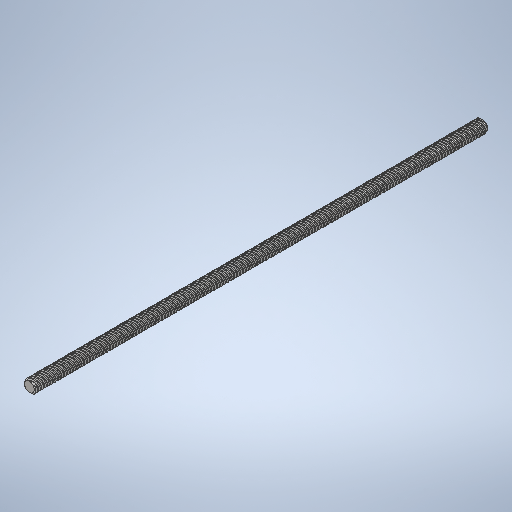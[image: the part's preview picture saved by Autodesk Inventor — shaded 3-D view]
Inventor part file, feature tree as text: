
AUTODESK INVENTOR PART (.ipt)
format: ipt  version: 2025.2 (Build 292293000, 293)  size: 1,360,384 bytes
history: native  units: mm
features: extrude x1, chamfer x1, other x1, pattern_circular x1
ambient origin geometry x8: Origin, YZ Plane, XZ Plane, XY Plane, X Axis, Y Axis, Z Axis, Center Point
bodies: Solid1 (feature_tree)
feature tree (4):
  extrude  "1000mm Rod"  Depth=285.0mm TaperAngle=0.0deg
  chamfer  "Chamfer1"  Distance=0.907143mm Angle=45.0deg
  other  "ACME Thread 2mm Pitch"
  pattern_circular  "4 Start"  [2 undecoded]
note: 2 required parameter values undecoded (feature->parameter linkage not recoverable at this tier; creation-order binding heuristic only, values carry confidence <= 0.55)
